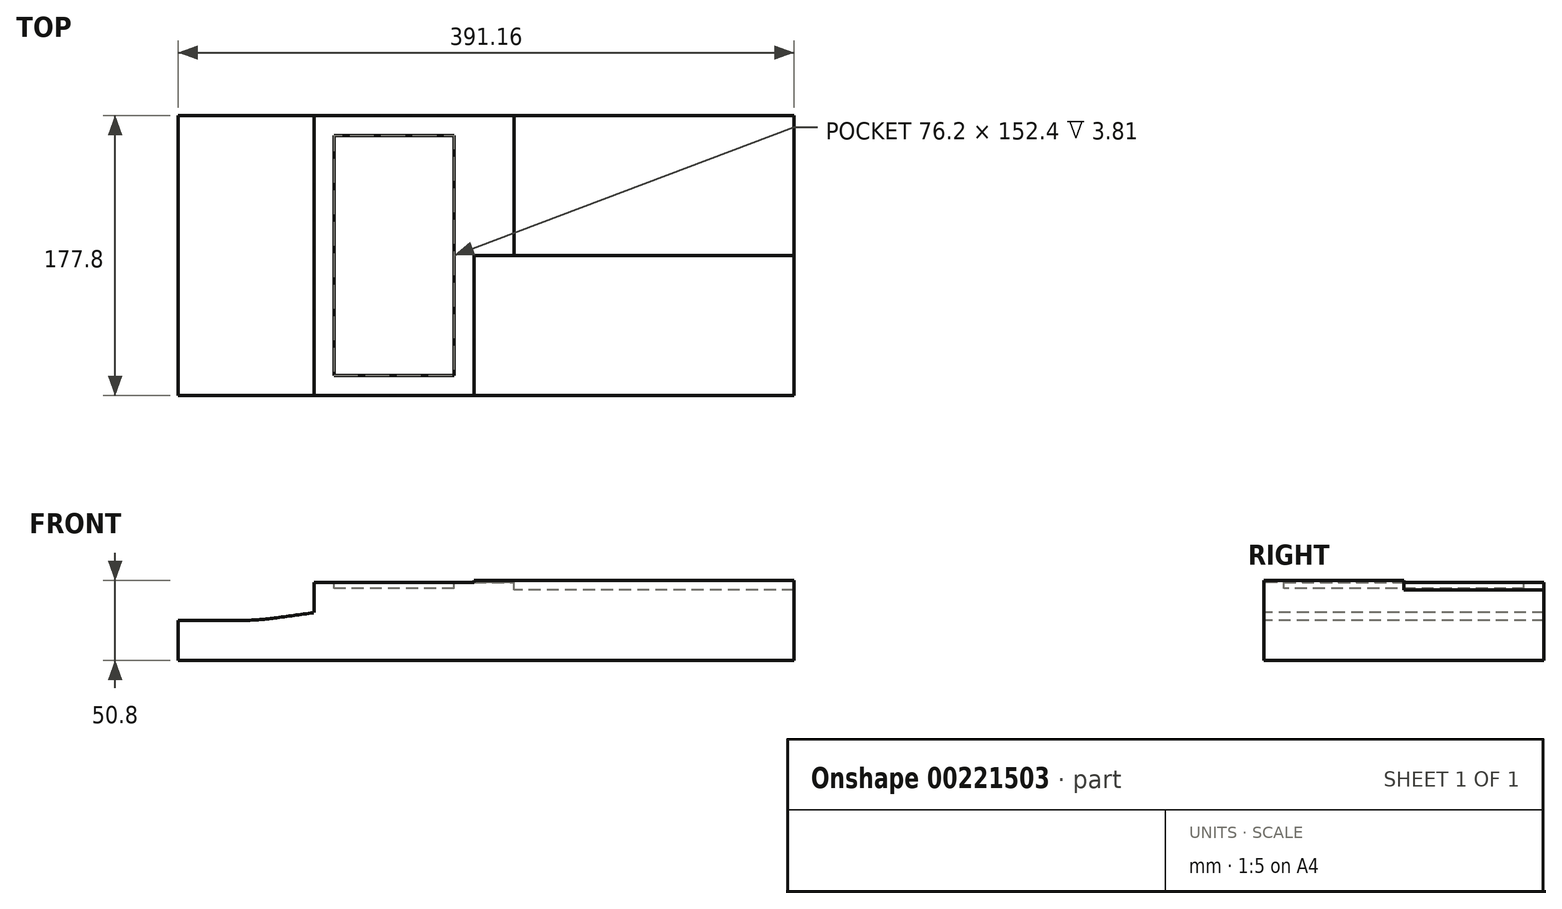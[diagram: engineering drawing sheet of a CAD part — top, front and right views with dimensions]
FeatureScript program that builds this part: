
annotation { "Feature Type Name" : "Feature", "Feature Type Description" : "" }
export const myFeature = defineFeature(function(context is Context, id is Id, definition is map)
    precondition{}
    {
        {
            var Q0;
            Q0=qCreatedBy(makeId("Top.planeOp"),FACE);
            var sketch = newSketch(context, id + "F0", { "sketchPlane" : qUnion([Q0])});
            skLineSegment(sketch, "E0.bottom", {"start": v(68.58, 88.9) * mm, "end": v(-68.58, 88.9) * mm});
            skLineSegment(sketch, "E0.top", {"start": v(68.58, -88.9) * mm, "end": v(-68.58, -88.9) * mm});
            skLineSegment(sketch, "E0.left", {"start": v(68.58, 88.9) * mm, "end": v(68.58, -88.9) * mm});
            skLineSegment(sketch, "E0.right", {"start": v(-68.58, 88.9) * mm, "end": v(-68.58, -88.9) * mm});
            skPoint(sketch, "E0.middle", {"position": v(0, 0) * mm});
            skSolve(sketch);
        }
        {
            var Q0;
            Q0 = qSketchRegion(id + "F0", true);
            extrude(context, id + "F1", {"entities" : qUnion([Q0]), "depth" : 25.4 * mm});
        }
        {
            var Q0;
            Q0=makeQuery(id+"F1.opExtrude","SWEPT_FACE",FACE,{"disambiguationData":[OSD([sQuery(id+"F0.wireOp",EDGE,"E0.top")])]});
            var sketch = newSketch(context, id + "F2", { "sketchPlane" : qUnion([Q0])});
            skLineSegment(sketch, "E1", {"start": v(-68.58, 0) * mm, "end": v(68.58, 25.4) * mm});
            skLineSegment(sketch, "E2", {"start": v(68.58, 25.4) * mm, "end": v(26.24, 59.22) * mm});
            skLineSegment(sketch, "E3", {"start": v(26.24, 59.22) * mm, "end": v(-97.1, 25.4) * mm});
            skLineSegment(sketch, "E4", {"start": v(-68.58, 0) * mm, "end": v(-97.1, 25.4) * mm});
            skSolve(sketch);
        }
        {
            var Q0;
            Q0 = qSketchRegion(id + "F2", true);
            extrude(context, id + "F3", {"entities" : qUnion([Q0]), "operationType" : NewBodyOperationType.REMOVE, "endBound" : BoundingType.THROUGH_ALL, "oppositeDirection" : true, "depth" : 25.4 * mm});
        }
        {
            var Q0;
            Q0=makeQuery(id+"F1.opExtrude","CAP_FACE",FACE,{"disambiguationData":[OSD([sQuery(id+"F0.wireOp",EDGE,"E0.bottom"),sQuery(id+"F0.wireOp",EDGE,"E0.top"),sQuery(id+"F0.wireOp",EDGE,"E0.left"),sQuery(id+"F0.wireOp",EDGE,"E0.right")])],"isStart":true});
            extrude(context, id + "F4", {"entities" : qUnion([Q0]), "operationType" : NewBodyOperationType.ADD, "depth" : 25.4 * mm});
        }
        {
            var Q0;
            {var subQ0=sQuery(id+"F0.wireOp",EDGE,"E0.left");Q0=makeQuery(id+"F4.boolean.opBoolean","MERGE",FACE,{"derivedFrom":[makeQuery(id+"F1.opExtrude","SWEPT_FACE",FACE,{"disambiguationData":[OSD([subQ0])]}),makeQuery(id+"F4.opExtrude","SWEPT_FACE",FACE,{"disambiguationData":[OSD([subQ0])]})]});}
            extrude(context, id + "F5", {"entities" : qUnion([Q0]), "operationType" : NewBodyOperationType.ADD, "depth" : 203.2 * mm});
        }
        {
            var Q0;
            {var subQ0=sQuery(id+"F0.wireOp",EDGE,"E0.bottom");Q0=makeQuery(id+"F5.boolean.opBoolean","MERGE",FACE,{"derivedFrom":[makeQuery(id+"F4.boolean.opBoolean","MERGE",FACE,{"derivedFrom":[makeQuery(id+"F1.opExtrude","SWEPT_FACE",FACE,{"disambiguationData":[OSD([subQ0])]}),makeQuery(id+"F4.opExtrude","SWEPT_FACE",FACE,{"disambiguationData":[OSD([subQ0])]})]}),makeQuery(id+"F5.opExtrude","SWEPT_FACE",FACE,{"disambiguationData":[OSD([subQ0,sQuery(id+"F0.wireOp",EDGE,"E0.left")])]})]});}
            var sketch = newSketch(context, id + "F6", { "sketchPlane" : qUnion([Q0])});
            skPoint(sketch, "E5.1.internal.snap0", {"position": v(0, 12.7) * mm});
            skFitSpline(sketch, "E5", {"points": [v(68.58, 0) * mm, v(0, 9.56) * mm, v(-68.58, 19.33) * mm], "startDerivative": vector(-137.18, 19.02) * mm, "endDerivative": vector(-137.14, 19.65) * mm});
            skFitSpline(sketch, "E6", {"points": [v(-68.58, 19.33) * mm, v(-68.58, 25.4) * mm], "startDerivative": vector(0, 6.07) * mm, "endDerivative": vector(0, 6.07) * mm});
            skLineSegment(sketch, "E7", {"start": v(68.58, 0) * mm, "end": v(68.58, 17.63) * mm});
            skLineSegment(sketch, "E8", {"start": v(68.58, 17.63) * mm, "end": v(-68.58, 25.4) * mm});
            skSolve(sketch);
        }
        {
            var Q0;
            Q0 = qSketchRegion(id + "F6", true);
            extrude(context, id + "F7", {"entities" : qUnion([Q0]), "operationType" : NewBodyOperationType.REMOVE, "endBound" : BoundingType.THROUGH_ALL, "oppositeDirection" : true, "depth" : 25.4 * mm});
        }
        {
            var Q0;
            Q0=makeQuery(id+"F7.boolean.opBoolean","COPY",FACE,{"derivedFrom":makeQuery(id+"F7.opExtrude","SWEPT_FACE",FACE,{"disambiguationData":[OSD([sQuery(id+"F6.wireOp",EDGE,"E6")])]})});
            var sketch = newSketch(context, id + "F8", { "sketchPlane" : qUnion([Q0])});
            skLineSegment(sketch, "E9.bottom", {"start": v(-88.9, 19.33) * mm, "end": v(0, 19.33) * mm});
            skLineSegment(sketch, "E9.top", {"start": v(-88.9, 25.4) * mm, "end": v(0, 25.4) * mm});
            skLineSegment(sketch, "E9.left", {"start": v(-88.9, 19.33) * mm, "end": v(-88.9, 25.4) * mm});
            skLineSegment(sketch, "E9.right", {"start": v(0, 19.33) * mm, "end": v(0, 25.4) * mm});
            skSolve(sketch);
        }
        {
            var Q0;
            Q0 = qSketchRegion(id + "F8", true);
            extrude(context, id + "F9", {"entities" : qUnion([Q0]), "operationType" : NewBodyOperationType.REMOVE, "endBound" : BoundingType.THROUGH_ALL, "oppositeDirection" : true, "depth" : 25.4 * mm});
        }
        {
            var Q0;
            Q0=makeQuery(id+"F9.boolean.opBoolean","MERGE",EDGE,{"derivedFrom":[makeQuery(id+"F7.boolean.opBoolean","COPY",EDGE,{"derivedFrom":makeQuery(id+"F7.opExtrude","SWEPT_EDGE",EDGE,{"disambiguationData":[OSD([sQuery(id+"F6.wireOp",EDGE,"E5"),sQuery(id+"F6.wireOp",EDGE,"E6")])]})}),makeQuery(id+"F9.opExtrude","CAP_EDGE",EDGE,{"disambiguationData":[OSD([sQuery(id+"F8.wireOp",EDGE,"E9.bottom")])],"isStart":true})]});
            fillet(context, id + "F10", {"entities" : qUnion([Q0]), "radius" : 127 * mm, "tangentPropagation" : true, "allowEdgeOverflow" : false});
        }
        {
            var Q0;
            Q0=makeQuery(id+"F4.opExtrude","SWEPT_FACE",FACE,{"disambiguationData":[OSD([sQuery(id+"F0.wireOp",EDGE,"E0.top"),sQuery(id+"F0.wireOp",EDGE,"E0.right"),sQuery(id+"F2.wireOp",EDGE,"E1"),sQuery(id+"F2.wireOp",EDGE,"E4")])]});
            extrude(context, id + "F11", {"entities" : qUnion([Q0]), "operationType" : NewBodyOperationType.ADD, "depth" : 50.8 * mm});
        }
        {
            var Q0;
            {var subQ0=sQuery(id+"F6.wireOp",EDGE,"E7");var subQ1=sQuery(id+"F6.wireOp",EDGE,"E5");var subQ2=sQuery(id+"F2.wireOp",EDGE,"E4");var subQ3=sQuery(id+"F2.wireOp",EDGE,"E1");var subQ4=sQuery(id+"F0.wireOp",EDGE,"E0.right");var subQ5=sQuery(id+"F0.wireOp",EDGE,"E0.top");var subQ6=sQuery(id+"F0.wireOp",EDGE,"E0.bottom");Q0=makeQuery(id+"F11.boolean.opBoolean","MERGE",EDGE,{"derivedFrom":[makeQuery(id+"F7.boolean.opBoolean","MERGE",EDGE,{"derivedFrom":[makeQuery(id+"F4.boolean.opBoolean","MERGE",EDGE,{"derivedFrom":[makeQuery(id+"F3.boolean.opBoolean","MERGE",EDGE,{"derivedFrom":[makeQuery(id+"F1.opExtrude","CAP_EDGE",EDGE,{"disambiguationData":[OSD([subQ4])],"isStart":true}),makeQuery(id+"F3.opExtrude","SWEPT_EDGE",EDGE,{"disambiguationData":[OSD([subQ5,subQ4,subQ3,subQ2])]})]}),makeQuery(id+"F4.opExtrude","CAP_EDGE",EDGE,{"disambiguationData":[OSD([subQ5,subQ4,subQ3,subQ2])],"isStart":true})]}),makeQuery(id+"F7.opExtrude","SWEPT_EDGE",EDGE,{"disambiguationData":[OSD([subQ6,subQ4,subQ3,subQ1,subQ0])]})]}),makeQuery(id+"F11.opExtrude","CAP_EDGE",EDGE,{"disambiguationData":[OSD([subQ6,subQ5,subQ4,subQ3,subQ2,subQ1,subQ0])],"isStart":true})]});}
            fillet(context, id + "F12", {"entities" : qUnion([Q0]), "radius" : 152.4 * mm, "tangentPropagation" : true, "allowEdgeOverflow" : false});
        }
        {
            var Q0;
            Q0=makeQuery(id+"F5.opExtrude","SWEPT_FACE",FACE,{"disambiguationData":[OSD([sQuery(id+"F0.wireOp",EDGE,"E0.top"),sQuery(id+"F0.wireOp",EDGE,"E0.left"),sQuery(id+"F2.wireOp",EDGE,"E1"),sQuery(id+"F2.wireOp",EDGE,"E2")])]});
            var sketch = newSketch(context, id + "F13", { "sketchPlane" : qUnion([Q0])});
            skLineSegment(sketch, "E10.bottom", {"start": v(68.58, -88.9) * mm, "end": v(-33.02, -88.9) * mm});
            skLineSegment(sketch, "E10.top", {"start": v(68.58, 88.9) * mm, "end": v(-33.02, 88.9) * mm});
            skLineSegment(sketch, "E10.left", {"start": v(68.58, -88.9) * mm, "end": v(68.58, 88.9) * mm});
            skLineSegment(sketch, "E10.right", {"start": v(-33.02, -88.9) * mm, "end": v(-33.02, 88.9) * mm});
            skSolve(sketch);
        }
        {
            var Q0;
            Q0 = qSketchRegion(id + "F13", true);
            extrude(context, id + "F14", {"entities" : qUnion([Q0]), "operationType" : NewBodyOperationType.ADD, "oppositeDirection" : true, "depth" : 50.8 * mm});
        }
        {
            var Q0;
            Q0=makeQuery(id+"F14.boolean.opBoolean","MERGE",FACE,{"derivedFrom":[makeQuery(id+"F5.opExtrude","SWEPT_FACE",FACE,{"disambiguationData":[OSD([sQuery(id+"F0.wireOp",EDGE,"E0.top"),sQuery(id+"F0.wireOp",EDGE,"E0.left"),sQuery(id+"F2.wireOp",EDGE,"E1"),sQuery(id+"F2.wireOp",EDGE,"E2")])]}),makeQuery(id+"F14.opExtrude","CAP_FACE",FACE,{"disambiguationData":[OSD([sQuery(id+"F13.wireOp",EDGE,"E10.bottom"),sQuery(id+"F13.wireOp",EDGE,"E10.top"),sQuery(id+"F13.wireOp",EDGE,"E10.left"),sQuery(id+"F13.wireOp",EDGE,"E10.right")])],"isStart":true})]});
            var sketch = newSketch(context, id + "F15", { "sketchPlane" : qUnion([Q0])});
            skLineSegment(sketch, "E11.bottom", {"start": v(55.88, 76.2) * mm, "end": v(-20.32, 76.2) * mm});
            skLineSegment(sketch, "E11.top", {"start": v(55.88, -76.2) * mm, "end": v(-20.32, -76.2) * mm});
            skLineSegment(sketch, "E11.left", {"start": v(55.88, 76.2) * mm, "end": v(55.88, -76.2) * mm});
            skLineSegment(sketch, "E11.right", {"start": v(-20.32, 76.2) * mm, "end": v(-20.32, -76.2) * mm});
            skPoint(sketch, "E11.middle", {"position": v(17.78, 0) * mm});
            skSolve(sketch);
        }
        {
            var Q0;
            Q0 = qSketchRegion(id + "F15", true);
            extrude(context, id + "F16", {"entities" : qUnion([Q0]), "operationType" : NewBodyOperationType.REMOVE, "oppositeDirection" : true, "depth" : 5.08 * mm});
        }
        {
            var Q0;
            Q0=makeQuery(id+"F14.opExtrude","SWEPT_FACE",FACE,{"disambiguationData":[OSD([sQuery(id+"F13.wireOp",EDGE,"E10.left")])]});
            extrude(context, id + "F17", {"entities" : qUnion([Q0]), "operationType" : NewBodyOperationType.ADD, "depth" : 25.4 * mm});
        }
        {
            var Q0;
            {var subQ0=sQuery(id+"F13.wireOp",EDGE,"E10.left");Q0=makeQuery(id+"F17.boolean.opBoolean","MERGE",FACE,{"derivedFrom":[makeQuery(id+"F14.boolean.opBoolean","MERGE",FACE,{"derivedFrom":[makeQuery(id+"F5.opExtrude","SWEPT_FACE",FACE,{"disambiguationData":[OSD([sQuery(id+"F0.wireOp",EDGE,"E0.top"),sQuery(id+"F0.wireOp",EDGE,"E0.left"),sQuery(id+"F2.wireOp",EDGE,"E1"),sQuery(id+"F2.wireOp",EDGE,"E2")])]}),makeQuery(id+"F14.opExtrude","CAP_FACE",FACE,{"disambiguationData":[OSD([sQuery(id+"F13.wireOp",EDGE,"E10.bottom"),sQuery(id+"F13.wireOp",EDGE,"E10.top"),subQ0,sQuery(id+"F13.wireOp",EDGE,"E10.right")])],"isStart":true})]}),makeQuery(id+"F17.opExtrude","SWEPT_FACE",FACE,{"disambiguationData":[OSD([subQ0])]})]});}
            var sketch = newSketch(context, id + "F18", { "sketchPlane" : qUnion([Q0])});
            skLineSegment(sketch, "E12", {"start": v(93.98, 0) * mm, "end": v(93.98, -88.9) * mm});
            skLineSegment(sketch, "E13", {"start": v(93.98, -88.9) * mm, "end": v(-33.02, -88.9) * mm});
            skLineSegment(sketch, "E14", {"start": v(-33.02, -88.9) * mm, "end": v(-33.02, 88.9) * mm});
            skLineSegment(sketch, "E15", {"start": v(-33.02, 88.9) * mm, "end": v(93.98, 88.9) * mm});
            skLineSegment(sketch, "E16", {"start": v(93.98, 88.9) * mm, "end": v(93.98, 0) * mm});
            skSolve(sketch);
        }
        {
            var Q0;
            Q0 = qSketchRegion(id + "F18", true);
            extrude(context, id + "F19", {"entities" : qUnion([Q0]), "operationType" : NewBodyOperationType.REMOVE, "oppositeDirection" : true, "depth" : 1.27 * mm});
        }
        {
            var Q0;
            Q0=makeQuery(id+"F19.boolean.opBoolean","COPY",FACE,{"derivedFrom":makeQuery(id+"F19.opExtrude","SWEPT_FACE",FACE,{"disambiguationData":[OSD([sQuery(id+"F18.wireOp",EDGE,"E12"),sQuery(id+"F18.wireOp",EDGE,"E16")])]})});
            extrude(context, id + "F20", {"entities" : qUnion([Q0]), "operationType" : NewBodyOperationType.ADD, "depth" : 25.4 * mm});
        }
    });
